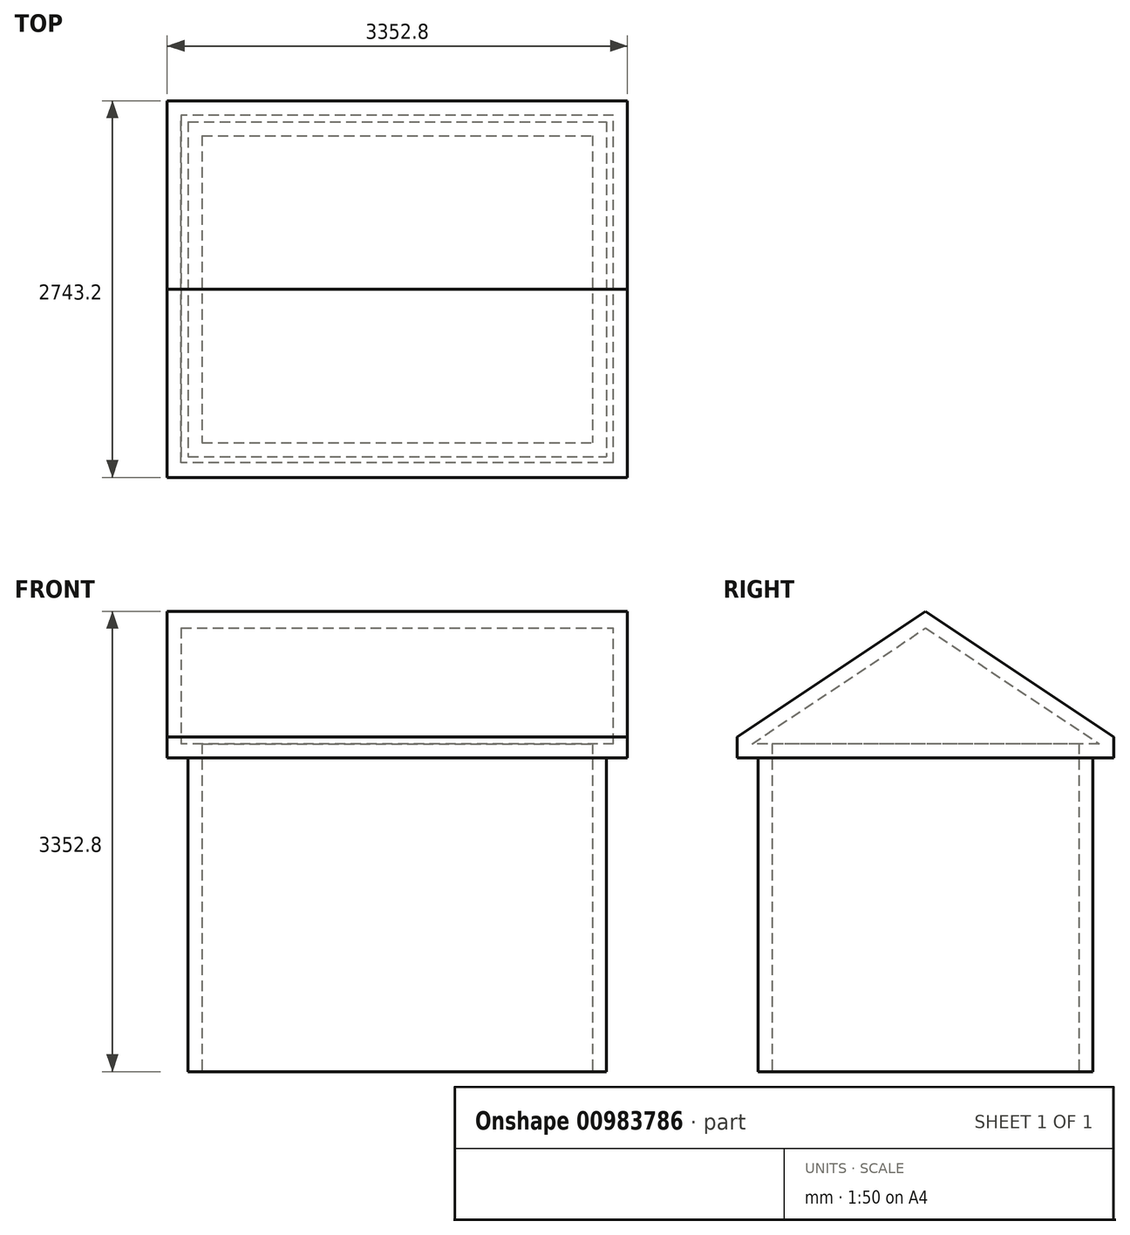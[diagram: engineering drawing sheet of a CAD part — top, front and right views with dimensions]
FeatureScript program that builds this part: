
annotation { "Feature Type Name" : "Feature", "Feature Type Description" : "" }
export const myFeature = defineFeature(function(context is Context, id is Id, definition is map)
    precondition{}
    {
        {
            var Q0;
            Q0=qCreatedBy(makeId("Top.planeOp"),FACE);
            var sketch = newSketch(context, id + "F0", { "sketchPlane" : qUnion([Q0])});
            skLineSegment(sketch, "E0.bottom", {"start": v(-3048, 736.93) * mm, "end": v(0, 736.93) * mm});
            skLineSegment(sketch, "E0.top", {"start": v(-3048, -1701.47) * mm, "end": v(0, -1701.47) * mm});
            skLineSegment(sketch, "E0.left", {"start": v(-3048, 736.93) * mm, "end": v(-3048, -1701.47) * mm});
            skLineSegment(sketch, "E0.right", {"start": v(0, 736.93) * mm, "end": v(0, -1701.47) * mm});
            skSolve(sketch);
        }
        {
            var Q0;
            Q0 = qSketchRegion(id + "F0", true);
            extrude(context, id + "F1", {"entities" : qUnion([Q0]), "depth" : 2286 * mm, "offsetDistance" : 25.4 * mm});
        }
        {
            var Q0;
            Q0=makeQuery(id+"F1.opExtrude","CAP_FACE",FACE,{"disambiguationData":[OSD([sQuery(id+"F0.wireOp",EDGE,"E0.bottom"),sQuery(id+"F0.wireOp",EDGE,"E0.top"),sQuery(id+"F0.wireOp",EDGE,"E0.left"),sQuery(id+"F0.wireOp",EDGE,"E0.right")])],"isStart":false});
            var sketch = newSketch(context, id + "F2", { "sketchPlane" : qUnion([Q0])});
            skLineSegment(sketch, "E1.0", {"start": v(-3200.4, 889.33) * mm, "end": v(-3200.4, -1853.87) * mm});
            skLineSegment(sketch, "E1.1", {"start": v(152.4, 889.33) * mm, "end": v(-3200.4, 889.33) * mm});
            skLineSegment(sketch, "E1.2", {"start": v(152.4, -1853.87) * mm, "end": v(152.4, 889.33) * mm});
            skLineSegment(sketch, "E1.3", {"start": v(-3200.4, -1853.87) * mm, "end": v(152.4, -1853.87) * mm});
            skSolve(sketch);
        }
        {
            var Q0;
            Q0 = qSketchRegion(id + "F2", true);
            extrude(context, id + "F3", {"entities" : qUnion([Q0]), "operationType" : NewBodyOperationType.ADD, "depth" : 152.4 * mm, "offsetDistance" : 25.4 * mm});
        }
        {
            var Q0;
            Q0=makeQuery(id+"F3.opExtrude","SWEPT_FACE",FACE,{"disambiguationData":[OSD([sQuery(id+"F2.wireOp",EDGE,"E1.2")])]});
            var sketch = newSketch(context, id + "F4", { "sketchPlane" : qUnion([Q0])});
            skLineSegment(sketch, "E2", {"start": v(-1853.87, 2438.4) * mm, "end": v(-482.27, 3352.8) * mm});
            skLineSegment(sketch, "E3", {"start": v(-482.27, 3352.8) * mm, "end": v(889.33, 2438.4) * mm});
            skLineSegment(sketch, "E4", {"start": v(889.33, 2438.4) * mm, "end": v(-1853.87, 2438.4) * mm});
            skLineSegment(sketch, "E5", {"start": v(-482.27, 2438.4) * mm, "end": v(-482.27, 3352.8) * mm});
            skSolve(sketch);
        }
        {
            var Q0;
            Q0 = qSketchRegion(id + "F4", true);
            var Q1;
            Q1=makeQuery(id+"F3.opExtrude","CAP_VERTEX",VERTEX,{"disambiguationData":[OSD([sQuery(id+"F2.wireOp",EDGE,"E1.0"),sQuery(id+"F2.wireOp",EDGE,"E1.3")])],"isStart":false});
            extrude(context, id + "F5", {"entities" : qUnion([Q0]), "operationType" : NewBodyOperationType.ADD, "endBound" : BoundingType.UP_TO_VERTEX, "oppositeDirection" : true, "depth" : 25.4 * mm, "endBoundEntityVertex" : qUnion([Q1]), "offsetDistance" : 25.4 * mm});
        }
        {
            var Q0;
            Q0=makeQuery(id+"F1.opExtrude","CAP_FACE",FACE,{"disambiguationData":[OSD([sQuery(id+"F0.wireOp",EDGE,"E0.bottom"),sQuery(id+"F0.wireOp",EDGE,"E0.top"),sQuery(id+"F0.wireOp",EDGE,"E0.left"),sQuery(id+"F0.wireOp",EDGE,"E0.right")])],"isStart":true});
            shell(context, id + "F6", {"entities" : qUnion([Q0]), "thickness" : 101.6 * mm});
        }
    });
